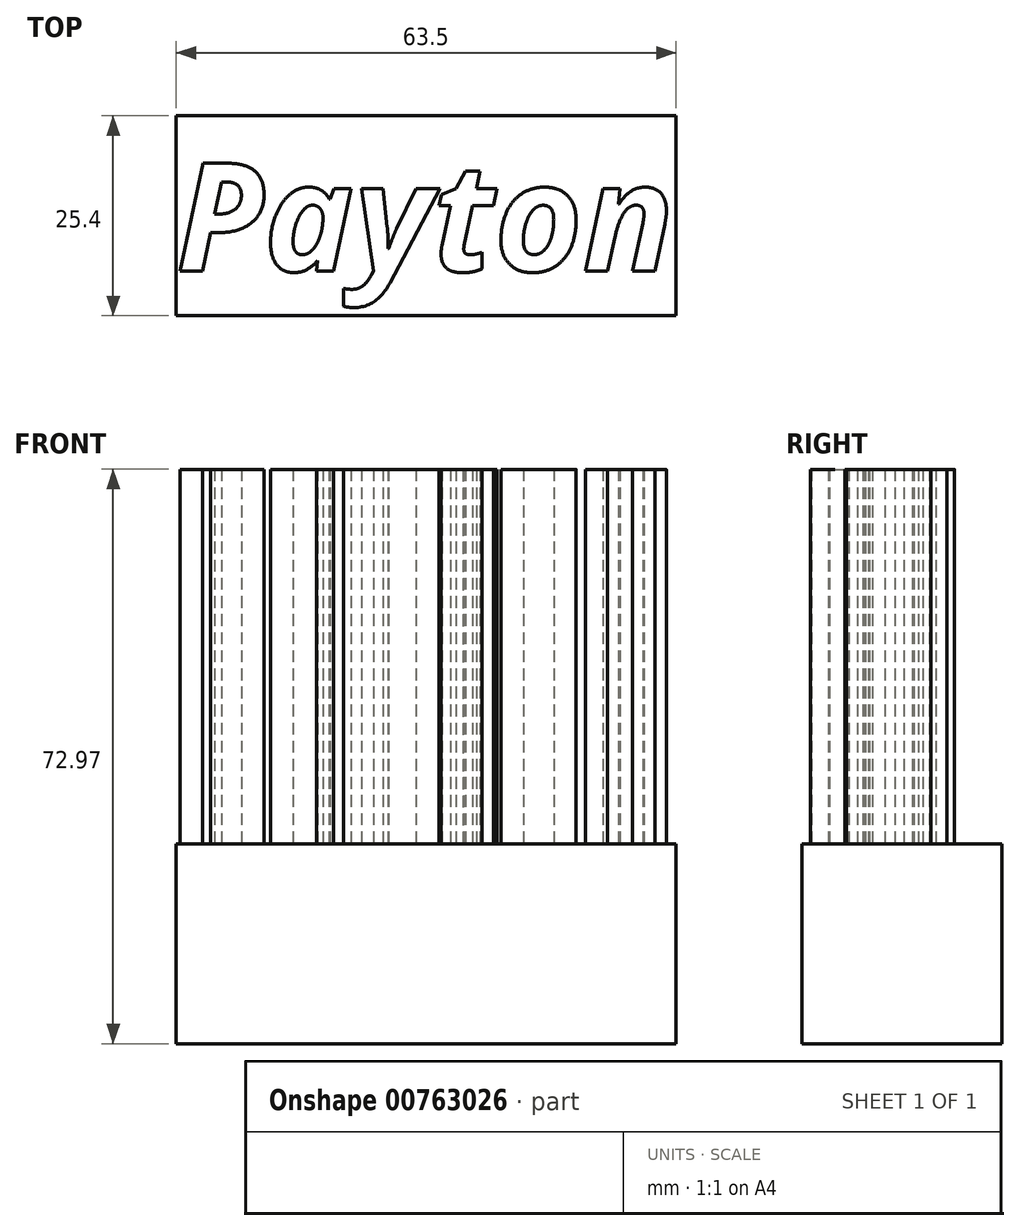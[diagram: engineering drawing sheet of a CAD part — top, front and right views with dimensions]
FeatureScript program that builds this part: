
annotation { "Feature Type Name" : "Feature", "Feature Type Description" : "" }
export const myFeature = defineFeature(function(context is Context, id is Id, definition is map)
    precondition{}
    {
        {
            var Q0;
            Q0=qCreatedBy(makeId("Top.planeOp"),FACE);
            var sketch = newSketch(context, id + "F0", { "sketchPlane" : qUnion([Q0])});
            skLineSegment(sketch, "E0.bottom", {"start": v(0, 0) * mm, "end": v(63.5, 0) * mm});
            skLineSegment(sketch, "E0.top", {"start": v(0, 25.4) * mm, "end": v(63.5, 25.4) * mm});
            skLineSegment(sketch, "E0.left", {"start": v(0, 0) * mm, "end": v(0, 25.4) * mm});
            skLineSegment(sketch, "E0.right", {"start": v(63.5, 0) * mm, "end": v(63.5, 25.4) * mm});
            skSolve(sketch);
        }
        {
            var Q0;
            Q0=makeQuery(id+"F0.imprint","IMPRINT",FACE,{"disambiguationData":[TD([[makeQuery(id+"F0.imprint","IMPRINT",EDGE,{"derivedFrom":sQuery(id+"F0.wireOp",EDGE,"E0.bottom")}),1.0]])]});
            var sketch = newSketch(context, id + "F1", { "sketchPlane" : qUnion([Q0])});
            skSolve(sketch);
        }
        {
            var Q0;
            Q0=makeQuery(id+"F1.imprint","IMPRINT",FACE,{"disambiguationData":[TD([[makeQuery(id+"F1.imprint","IMPRINT",EDGE,{"derivedFrom":makeQuery(id+"F0.imprint","IMPRINT",EDGE,{"derivedFrom":sQuery(id+"F0.wireOp",EDGE,"E0.bottom")})}),1.0]])]});
            var sketch = newSketch(context, id + "F2", { "sketchPlane" : qUnion([Q0])});
            skSolve(sketch);
        }
        {
            var Q0;
            Q0=makeQuery(id+"F1.imprint","IMPRINT",FACE,{"disambiguationData":[TD([[makeQuery(id+"F1.imprint","IMPRINT",EDGE,{"derivedFrom":makeQuery(id+"F0.imprint","IMPRINT",EDGE,{"derivedFrom":sQuery(id+"F0.wireOp",EDGE,"E0.bottom")})}),1.0]])]});
            var sketch = newSketch(context, id + "F3", { "sketchPlane" : qUnion([Q0])});
            skText(sketch, "E1", { "text": "Payton ", "fontName": "OpenSans-BoldItalic.ttf"});
            const initialGuessF3  = {"E1": [0, 0.00566, 1, 0, 0.01383]};
            skSetInitialGuess(sketch, initialGuessF3);
            skSolve(sketch);
        }
        {
            var Q0;
            Q0 = qSketchRegion(id + "F0", true);
            extrude(context, id + "F4", {"entities" : qUnion([Q0]), "depth" : 25.4 * mm, "offsetDistance" : 25.4 * mm});
        }
        {
            var Q0;
            Q0 = qSketchRegion(id + "F2", true);
            var Q1;
            Q1 = qSketchRegion(id + "F3", true);
            extrude(context, id + "F5", {"entities" : qUnion([Q0, Q1]), "operationType" : NewBodyOperationType.ADD, "endBound" : BoundingType.THROUGH_ALL, "depth" : 12.7 * mm, "offsetDistance" : 25.4 * mm});
        }
    });
